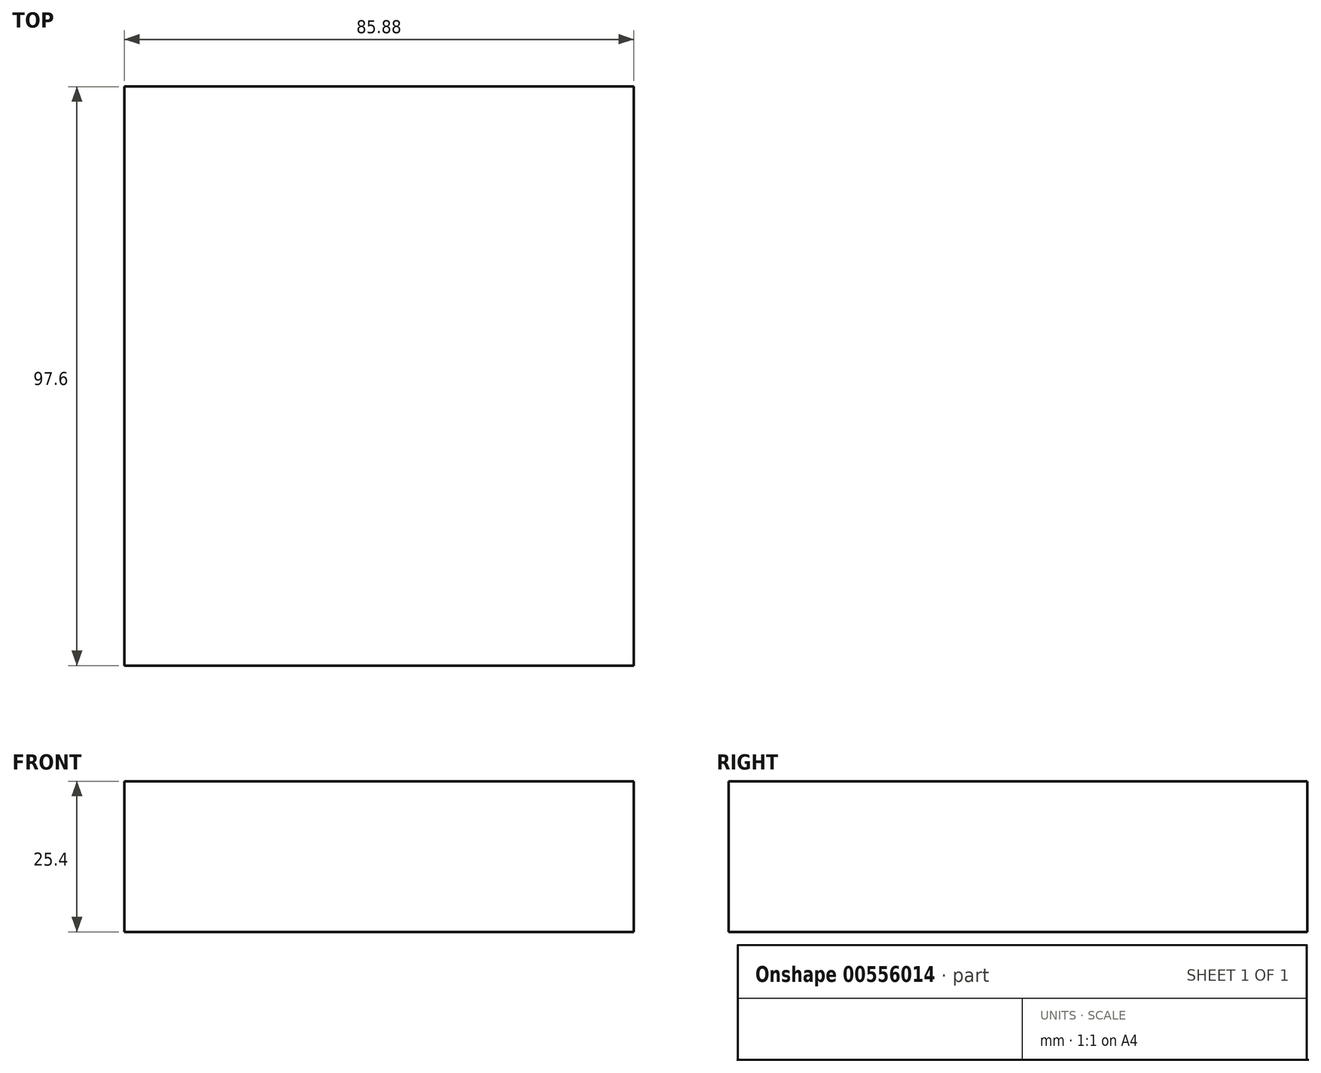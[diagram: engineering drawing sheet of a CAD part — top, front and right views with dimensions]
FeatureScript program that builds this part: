
annotation { "Feature Type Name" : "Feature", "Feature Type Description" : "" }
export const myFeature = defineFeature(function(context is Context, id is Id, definition is map)
    precondition{}
    {
        {
            var Q0;
            Q0=qCreatedBy(makeId("Top.planeOp"),FACE);
            var sketch = newSketch(context, id + "F0", { "sketchPlane" : qUnion([Q0])});
            skLineSegment(sketch, "E0.bottom", {"start": v(42.94, 48.8) * mm, "end": v(-42.94, 48.8) * mm});
            skLineSegment(sketch, "E0.top", {"start": v(42.94, -48.8) * mm, "end": v(-42.94, -48.8) * mm});
            skLineSegment(sketch, "E0.left", {"start": v(42.94, 48.8) * mm, "end": v(42.94, -48.8) * mm});
            skLineSegment(sketch, "E0.right", {"start": v(-42.94, 48.8) * mm, "end": v(-42.94, -48.8) * mm});
            skPoint(sketch, "E0.middle", {"position": v(0, 0) * mm});
            skSolve(sketch);
        }
        {
            var Q0;
            Q0 = qSketchRegion(id + "F0", true);
            extrude(context, id + "F1", {"entities" : qUnion([Q0]), "endBound" : BoundingType.SYMMETRIC, "depth" : 25.4 * mm, "offsetDistance" : 25.4 * mm});
        }
    });
